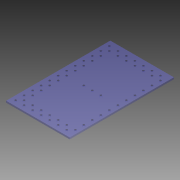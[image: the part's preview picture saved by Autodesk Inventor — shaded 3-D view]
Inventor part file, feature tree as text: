
AUTODESK INVENTOR PART (.ipt)
format: ipt  version: 2014 SP2 (Build 180246200, 246)  size: 239,616 bytes
history: native  units: in
note: dims shown in document units (in); Inventor stores cm internally (conversion verified against a paired STEP export)
features: extrude x6, sketch x5, pattern_linear x3
ambient origin geometry x8: Origin, YZ Plane, XZ Plane, XY Plane, X Axis, Y Axis, Z Axis, Center Point
bodies: Solid1 (feature_tree)
feature tree (14):
  sketch  "Sketch1"  dims[d0=7.9921in d1=4.8486in]
  extrude  "Extrusion1"  Depth=4.8486in
  extrude  "Extrusion2"  Depth=7.7in
  pattern_linear  "Rectangular Pattern1"  Spacing1=0.315in  [1 undecoded]
  pattern_linear  "Rectangular Pattern2"  Count1=7 Spacing1=0.63in
  extrude  "Extrusion3"  Depth=0.125in
  extrude  "Extrusion4"  Depth=0.125in
  extrude  "Extrusion5"  Depth=0.125in
  extrude  "Extrusion6"  Depth=0.125in
  pattern_linear  "Rectangular Pattern3"  Spacing1=0.146in  [1 undecoded]
  sketch  "Sketch2"  dims[d2=4.7in d3=7.7in]
  sketch  "Sketch3"  dims[d4=3.4645in]
  sketch  "Sketch4"  dims[d5=6.929in]
  sketch  "Sketch5"  dims[d6=0.63in d7=0.315in d8=2.7559in d10=0.63in d11=0.3937in d13=1.0in d15=0.315in d16=0.146in d17=0.146in d18=0.315in d19=0.146in d20=0.125in d21=0.0in d22=0.125in d23=0.0in d24=2.7559in d26=0.63in d27=4.7244in d29=0.63in d30=0.125in d31=0.0in d32=2.7559in d34=0.63in d35=0.3937in d37=1.0in d39=0.125in d40=0.0in d41=0.146in d42=0.146in d43=0.146in d44=1.0in d45=0.0in d46=0.146in d47=1.0in d48=0.0in d49=3.5433in d51=0.63in]
note: 2 required parameter values undecoded (feature->parameter linkage not recoverable at this tier; creation-order binding heuristic only, values carry confidence <= 0.55)
